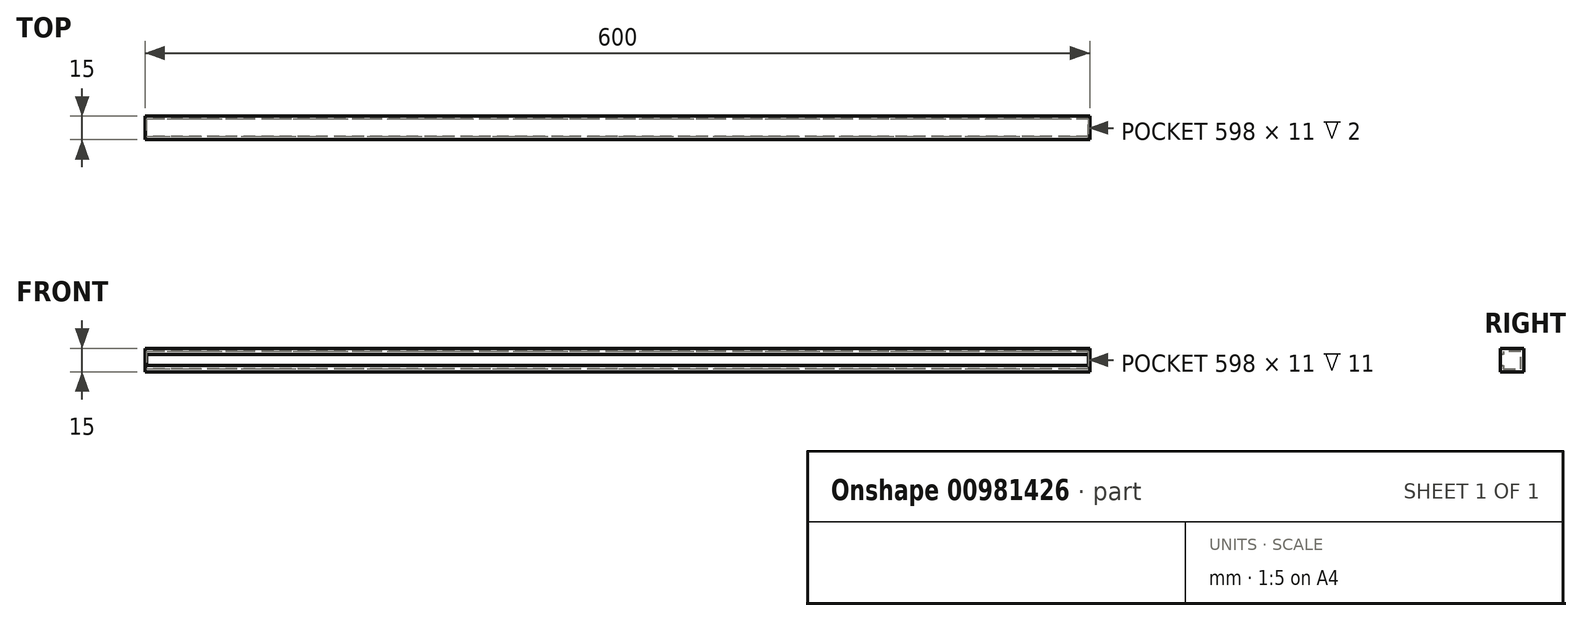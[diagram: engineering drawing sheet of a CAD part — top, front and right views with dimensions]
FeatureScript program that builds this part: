
annotation { "Feature Type Name" : "Feature", "Feature Type Description" : "" }
export const myFeature = defineFeature(function(context is Context, id is Id, definition is map)
    precondition{}
    {
        {
            var Q0;
            Q0=qCreatedBy(makeId("Right.planeOp"),FACE);
            var sketch = newSketch(context, id + "F0", { "sketchPlane" : qUnion([Q0])});
            skLineSegment(sketch, "E0.bottom", {"start": v(-7.5, 7.5) * mm, "end": v(7.5, 7.5) * mm});
            skLineSegment(sketch, "E0.top", {"start": v(-7.5, -7.5) * mm, "end": v(7.5, -7.5) * mm});
            skLineSegment(sketch, "E0.left", {"start": v(-7.5, 7.5) * mm, "end": v(-7.5, 3.5) * mm});
            skLineSegment(sketch, "E0.right", {"start": v(7.5, 7.5) * mm, "end": v(7.5, -7.5) * mm});
            skPoint(sketch, "E0.middle", {"position": v(0, 0) * mm});
            skLineSegment(sketch, "E1", {"start": v(-7.5, -3.5) * mm, "end": v(-5.5, -3.5) * mm});
            skLineSegment(sketch, "E2", {"start": v(-5.5, -3.5) * mm, "end": v(-5.5, -5.5) * mm});
            skLineSegment(sketch, "E3", {"start": v(-5.5, -5.5) * mm, "end": v(5.5, -5.5) * mm});
            skLineSegment(sketch, "E4", {"start": v(5.5, -5.5) * mm, "end": v(5.5, 5.5) * mm});
            skLineSegment(sketch, "E5", {"start": v(5.5, 5.5) * mm, "end": v(-5.5, 5.5) * mm});
            skLineSegment(sketch, "E6", {"start": v(-5.5, 5.5) * mm, "end": v(-5.5, 3.5) * mm});
            skLineSegment(sketch, "E7", {"start": v(-5.5, 3.5) * mm, "end": v(-7.5, 3.5) * mm});
            skLineSegment(sketch, "E8.trimOffspring", {"start": v(-7.5, -3.5) * mm, "end": v(-7.5, -7.5) * mm});
            skSolve(sketch);
        }
        {
            var Q0;
            Q0=makeQuery(id+"F0.imprint","IMPRINT",FACE,{"disambiguationData":[TD([[makeQuery(id+"F0.imprint","IMPRINT",EDGE,{"derivedFrom":sQuery(id+"F0.wireOp",EDGE,"E0.bottom")}),-1.0]])]});
            extrude(context, id + "F1", {"entities" : qUnion([Q0]), "endBound" : BoundingType.SYMMETRIC, "depth" : 598 * mm, "offsetDistance" : 25 * mm});
        }
        {
            var Q0;
            Q0=makeQuery(id+"F1.opExtrude","CAP_FACE",FACE,{"disambiguationData":[OSD([sQuery(id+"F0.wireOp",EDGE,"E0.bottom"),sQuery(id+"F0.wireOp",EDGE,"E0.top"),sQuery(id+"F0.wireOp",EDGE,"E0.left"),sQuery(id+"F0.wireOp",EDGE,"E0.right"),sQuery(id+"F0.wireOp",EDGE,"E1"),sQuery(id+"F0.wireOp",EDGE,"E2"),sQuery(id+"F0.wireOp",EDGE,"E3"),sQuery(id+"F0.wireOp",EDGE,"E4"),sQuery(id+"F0.wireOp",EDGE,"E5"),sQuery(id+"F0.wireOp",EDGE,"E6"),sQuery(id+"F0.wireOp",EDGE,"E7"),sQuery(id+"F0.wireOp",EDGE,"E8.trimOffspring")])],"isStart":false});
            cPlane(context, id + "F2", {"entities" : qUnion([Q0]), "cplaneType" : CPlaneType.OFFSET, "offset" : 0 * mm, "width" : 150 * mm, "height" : 150 * mm});
        }
        {
            var Q0;
            Q0=qCreatedBy(id+"F2.planeOp",FACE);
            var sketch = newSketch(context, id + "F3", { "sketchPlane" : qUnion([Q0])});
            skLineSegment(sketch, "E9.bottom", {"start": v(-7.5, 7.5) * mm, "end": v(7.5, 7.5) * mm});
            skLineSegment(sketch, "E9.top", {"start": v(-7.5, -7.5) * mm, "end": v(7.5, -7.5) * mm});
            skLineSegment(sketch, "E9.left", {"start": v(-7.5, 7.5) * mm, "end": v(-7.5, -7.5) * mm});
            skLineSegment(sketch, "E9.right", {"start": v(7.5, 7.5) * mm, "end": v(7.5, -7.5) * mm});
            skPoint(sketch, "E9.middle", {"position": v(0, 0) * mm});
            skSolve(sketch);
        }
        {
            var Q0;
            Q0=makeQuery(id+"F3.imprint","IMPRINT",FACE,{"disambiguationData":[TD([[makeQuery(id+"F3.imprint","IMPRINT",EDGE,{"derivedFrom":sQuery(id+"F3.wireOp",EDGE,"E9.bottom")}),-1.0]])]});
            extrude(context, id + "F4", {"entities" : qUnion([Q0]), "operationType" : NewBodyOperationType.ADD, "depth" : 1 * mm, "offsetDistance" : 25 * mm});
        }
        {
            var Q0;
            Q0=makeQuery(id+"F1.opExtrude","CAP_FACE",FACE,{"disambiguationData":[OSD([sQuery(id+"F0.wireOp",EDGE,"E0.bottom"),sQuery(id+"F0.wireOp",EDGE,"E0.top"),sQuery(id+"F0.wireOp",EDGE,"E0.left"),sQuery(id+"F0.wireOp",EDGE,"E0.right"),sQuery(id+"F0.wireOp",EDGE,"E1"),sQuery(id+"F0.wireOp",EDGE,"E2"),sQuery(id+"F0.wireOp",EDGE,"E3"),sQuery(id+"F0.wireOp",EDGE,"E4"),sQuery(id+"F0.wireOp",EDGE,"E5"),sQuery(id+"F0.wireOp",EDGE,"E6"),sQuery(id+"F0.wireOp",EDGE,"E7"),sQuery(id+"F0.wireOp",EDGE,"E8.trimOffspring")])],"isStart":true});
            cPlane(context, id + "F5", {"entities" : qUnion([Q0]), "cplaneType" : CPlaneType.OFFSET, "offset" : 0 * mm, "width" : 150 * mm, "height" : 150 * mm});
        }
        {
            var Q0;
            Q0=qCreatedBy(id+"F5.planeOp",FACE);
            var sketch = newSketch(context, id + "F6", { "sketchPlane" : qUnion([Q0])});
            skLineSegment(sketch, "E10.bottom", {"start": v(-7.5, 7.5) * mm, "end": v(7.5, 7.5) * mm});
            skLineSegment(sketch, "E10.top", {"start": v(-7.5, -7.5) * mm, "end": v(7.5, -7.5) * mm});
            skLineSegment(sketch, "E10.left", {"start": v(-7.5, 7.5) * mm, "end": v(-7.5, -7.5) * mm});
            skLineSegment(sketch, "E10.right", {"start": v(7.5, 7.5) * mm, "end": v(7.5, -7.5) * mm});
            skPoint(sketch, "E10.middle", {"position": v(0, 0) * mm});
            skSolve(sketch);
        }
        {
            var Q0;
            Q0 = qSketchRegion(id + "F6", true);
            extrude(context, id + "F7", {"entities" : qUnion([Q0]), "operationType" : NewBodyOperationType.ADD, "depth" : 1 * mm, "offsetDistance" : 25 * mm});
        }
        {
            var Q0;
            Q0=makeQuery(id+"F7.boolean.opBoolean","MERGE",FACE,{"derivedFrom":[makeQuery(id+"F4.boolean.opBoolean","MERGE",FACE,{"derivedFrom":[makeQuery(id+"F1.opExtrude","SWEPT_FACE",FACE,{"disambiguationData":[OSD([sQuery(id+"F0.wireOp",EDGE,"E0.bottom")])]}),makeQuery(id+"F4.opExtrude","SWEPT_FACE",FACE,{"disambiguationData":[OSD([sQuery(id+"F3.wireOp",EDGE,"E9.bottom")])]})]}),makeQuery(id+"F7.opExtrude","SWEPT_FACE",FACE,{"disambiguationData":[OSD([sQuery(id+"F6.wireOp",EDGE,"E10.bottom")])]})]});
            cPlane(context, id + "F8", {"entities" : qUnion([Q0]), "cplaneType" : CPlaneType.OFFSET, "offset" : 0 * mm, "width" : 150 * mm, "height" : 150 * mm});
        }
        {
            var Q0;
            Q0=qCreatedBy(id+"F8.planeOp",FACE);
            var sketch = newSketch(context, id + "F9", { "sketchPlane" : qUnion([Q0])});
            skPoint(sketch, "E11", {"position": v(-200, 0) * mm});
            skCircle(sketch, "E12", {"center": v(-200, 0) * mm, "radius": 3.5 * mm});
            skSolve(sketch);
        }
        {
            var Q0;
            Q0=sQuery(id+"F9.wireOp",EDGE,"E12");
            extrude(context, id + "F10", {"bodyType" : ToolBodyType.SURFACE, "surfaceEntities" : qUnion([Q0]), "depth" : 5 * mm, "offsetDistance" : 25 * mm});
        }
        {
            var Q0;
            Q0=makeQuery(id+"F7.boolean.opBoolean","MERGE",FACE,{"derivedFrom":[makeQuery(id+"F4.boolean.opBoolean","MERGE",FACE,{"derivedFrom":[makeQuery(id+"F1.opExtrude","SWEPT_FACE",FACE,{"disambiguationData":[OSD([sQuery(id+"F0.wireOp",EDGE,"E0.top")])]}),makeQuery(id+"F4.opExtrude","SWEPT_FACE",FACE,{"disambiguationData":[OSD([sQuery(id+"F3.wireOp",EDGE,"E9.top")])]})]}),makeQuery(id+"F7.opExtrude","SWEPT_FACE",FACE,{"disambiguationData":[OSD([sQuery(id+"F6.wireOp",EDGE,"E10.top")])]})]});
            cPlane(context, id + "F11", {"entities" : qUnion([Q0]), "cplaneType" : CPlaneType.OFFSET, "offset" : 0 * mm, "width" : 150 * mm, "height" : 150 * mm});
        }
        {
            var Q0;
            Q0=qCreatedBy(id+"F11.planeOp",FACE);
            var sketch = newSketch(context, id + "F12", { "sketchPlane" : qUnion([Q0])});
            skPoint(sketch, "E13", {"position": v(-200, 0) * mm});
            skCircle(sketch, "E14", {"center": v(-200, 0) * mm, "radius": 3.5 * mm});
            skSolve(sketch);
        }
        {
            var Q0;
            Q0=sQuery(id+"F12.wireOp",EDGE,"E14");
            extrude(context, id + "F13", {"bodyType" : ToolBodyType.SURFACE, "surfaceEntities" : qUnion([Q0]), "depth" : 5 * mm, "offsetDistance" : 25 * mm});
        }
    });
